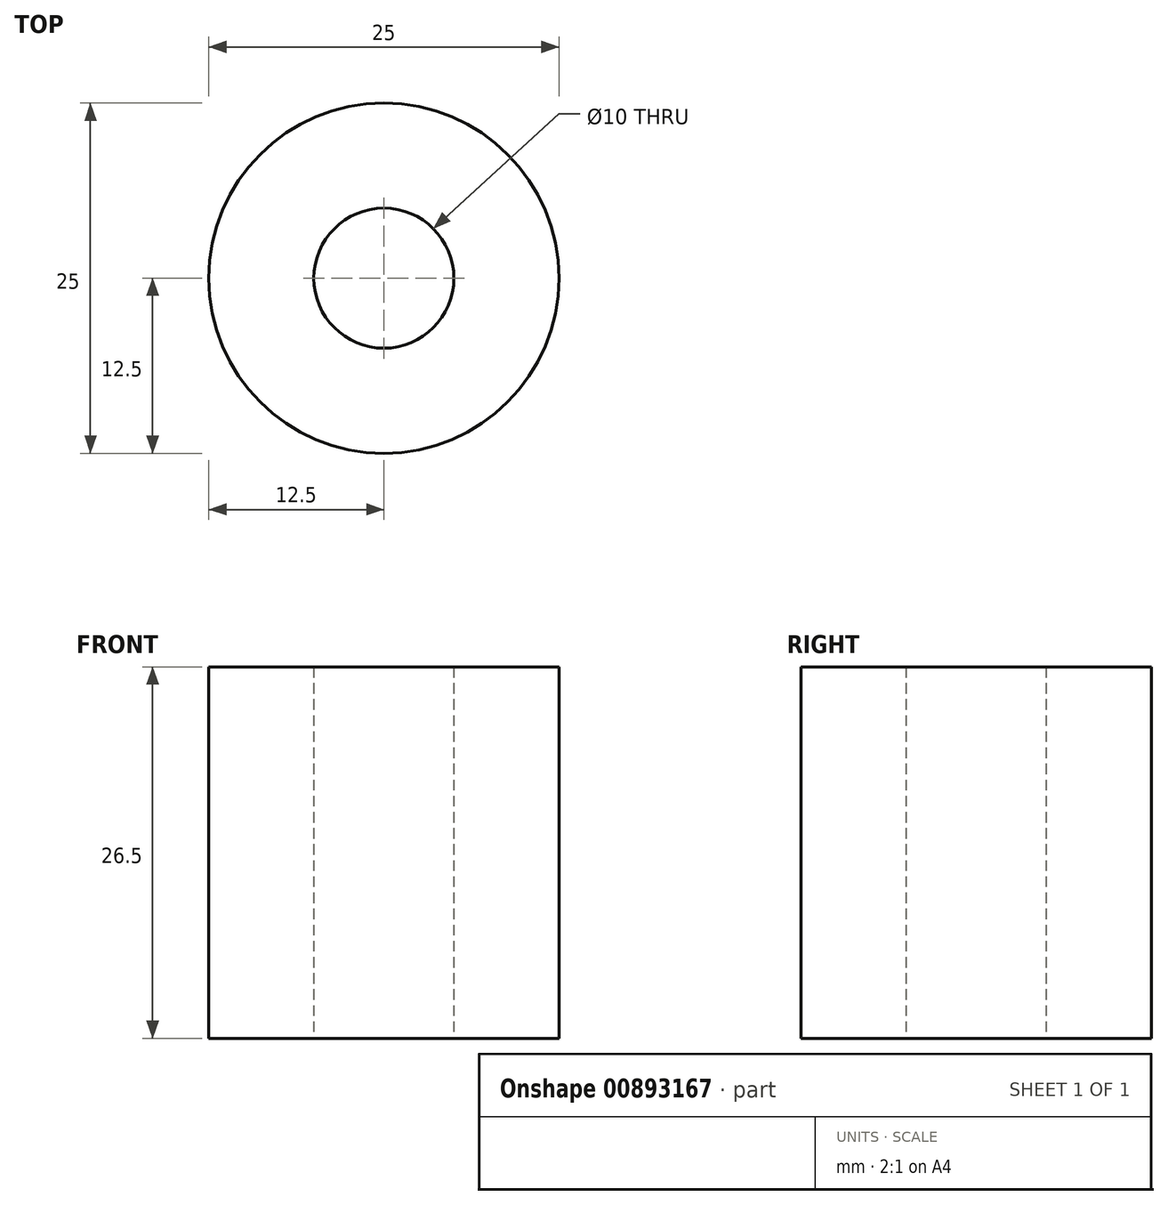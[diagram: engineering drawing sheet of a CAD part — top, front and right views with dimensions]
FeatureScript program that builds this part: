
annotation { "Feature Type Name" : "Feature", "Feature Type Description" : "" }
export const myFeature = defineFeature(function(context is Context, id is Id, definition is map)
    precondition{}
    {
        {
            var Q0;
            Q0=qCreatedBy(makeId("Top.planeOp"),FACE);
            var sketch = newSketch(context, id + "F0", { "sketchPlane" : qUnion([Q0])});
            skCircle(sketch, "E0", {"center": v(0, 0) * mm, "radius": 5 * mm});
            skCircle(sketch, "E1", {"center": v(0, 0) * mm, "radius": 12.5 * mm});
            skSolve(sketch);
        }
        {
            var Q0;
            Q0=makeQuery(id+"F0.imprint","IMPRINT",FACE,{"disambiguationData":[TD([[makeQuery(id+"F0.imprint","IMPRINT",EDGE,{"derivedFrom":sQuery(id+"F0.wireOp",EDGE,"E0")}),-1.0]])]});
            extrude(context, id + "F1", {"entities" : qUnion([Q0]), "depth" : 26.5 * mm, "offsetDistance" : 25 * mm});
        }
    });
